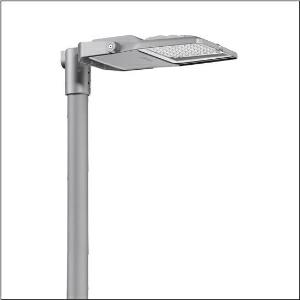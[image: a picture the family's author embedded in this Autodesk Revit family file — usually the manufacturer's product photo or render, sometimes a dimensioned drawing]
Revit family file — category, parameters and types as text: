
# Revit family: floodlight_fl_21_iq_mini___pl61_5xa7771d4c3a_f55b
name_source: partatom
category: Lighting Fixtures
units: mm (PartAtom-declared; Revit-internal decimal feet)

## family parameters
Cut with Voids When Loaded = No
Host = Face
Light Source = No
Part Type = Normal
Room Calculation Point = No
Round Connector Dimension = Use Diameter
Shared = No

## types (1)
- --- (1 x LED, 18260 lm, 143 W, 4000K)
    Apparent Load = 143 VA
    CIE Flux Codes = 33 65 98 100 100
    Color Rendering = 70
    Color Temperature = 4000K
    Default Elevation = 1800 mm
    Description = Floodlight FL 21 iQ mini, floodlight, primary light control with lens, of PMMA, primary optical cover: protective disc, of toughened safety glass, transparent, light distribution: PL61, light emission: direct distribution, installation type: surface-mounted, LED, High Power LED, rated luminous flux: 18.260lm, luminous efficacy: 128lm/W, light colour: 740, colour temperature: 4000K, control: Auto-Match, Temp-Guard, Lumen-Switch, Night-Set, Smart-Wire, Light-Fading, Desk-Remote (wireless, voltage-free reading and setting of iQ features in the workshop via application-optimized NFC function/RFID function), optimised constant luminous flux control (CLO 2.0), with terminal, 6-pole, mains connection: 220..240V, AC, 50/60Hz, start of lifetime: 143W, end of service life: 152W, reduction: 61W, luminaire housing, of diecast aluminium, powder-coated, Siteco® metallic grey (DB 702S), corrosivity category C5 mid according to DIN EN ISO 12944, sealing non-destructively replaceable, please order mast flange separately, mast bracket, of steel, galvanised, powder-coated, Siteco® metallic grey (DB 702S), protection rating (complete): IP66, insulation class (complete): insulation class II (safety insulation), certification: CE, ENEC, VDE, protection symbol: D, impact resistance: IK08, permissible operating ambient temperature: -40..+40°C, permissible operating ambient temperature for outdoor applications: -40..+50°C, standard: DIN EN 12944, LABS conformity tested according to VDMA 24364:2018-05, packaging unit: 1 piece

Light Distribution: PL61
    Height = 70 mm
    Lamp = 1 x LED
    Lamp Light Flux = 18260 lm
    Lamp Power = 143 W
    Lamp count = 1
    Length = 485 mm
    Luminous efficacy = 128 lm/W
    Manufacturer = Siteco
    ModVariant = No
    Model = 5XA7771D4C3A
    Number of Poles = 1
    OnlyDefault = Yes
    Power Factor = 1
    Product Name = Floodlight FL 21 iQ mini | PL61
    Product group = floodlight | pylon annexe
    ProductGroupID = 6200
    Protection Class = Protection class II
    Protection Degree = IP 66
    RLX_Detail_Level = 1
    RLX_Emergency_Light_Flux = 0 lm
    RLX_Emergency_Type = 0
    RLX_Emergency_Type_DB = No
    RlxData = <blob elided: 101629 chars, md5=a5ff5913>
    Socket = socket
    Standby Power = 0 W
    System Light Flux = 18260 lm
    System Power = 143 W
    Type Comments = factory setting: luminous flux: 100 % | dim-lin: 254 | 730 mA
    Type Image = l_1007125.jpg
    URL = http://relux.com
    VarID = @adj_105679
    Voltage = 0 V
    Weight = 0.00 kg
    Width = 337 mm

## geometry (parser evidence)
native form markers: Blend x4, Sweep x12
no freeform markers — native parametric forms only
